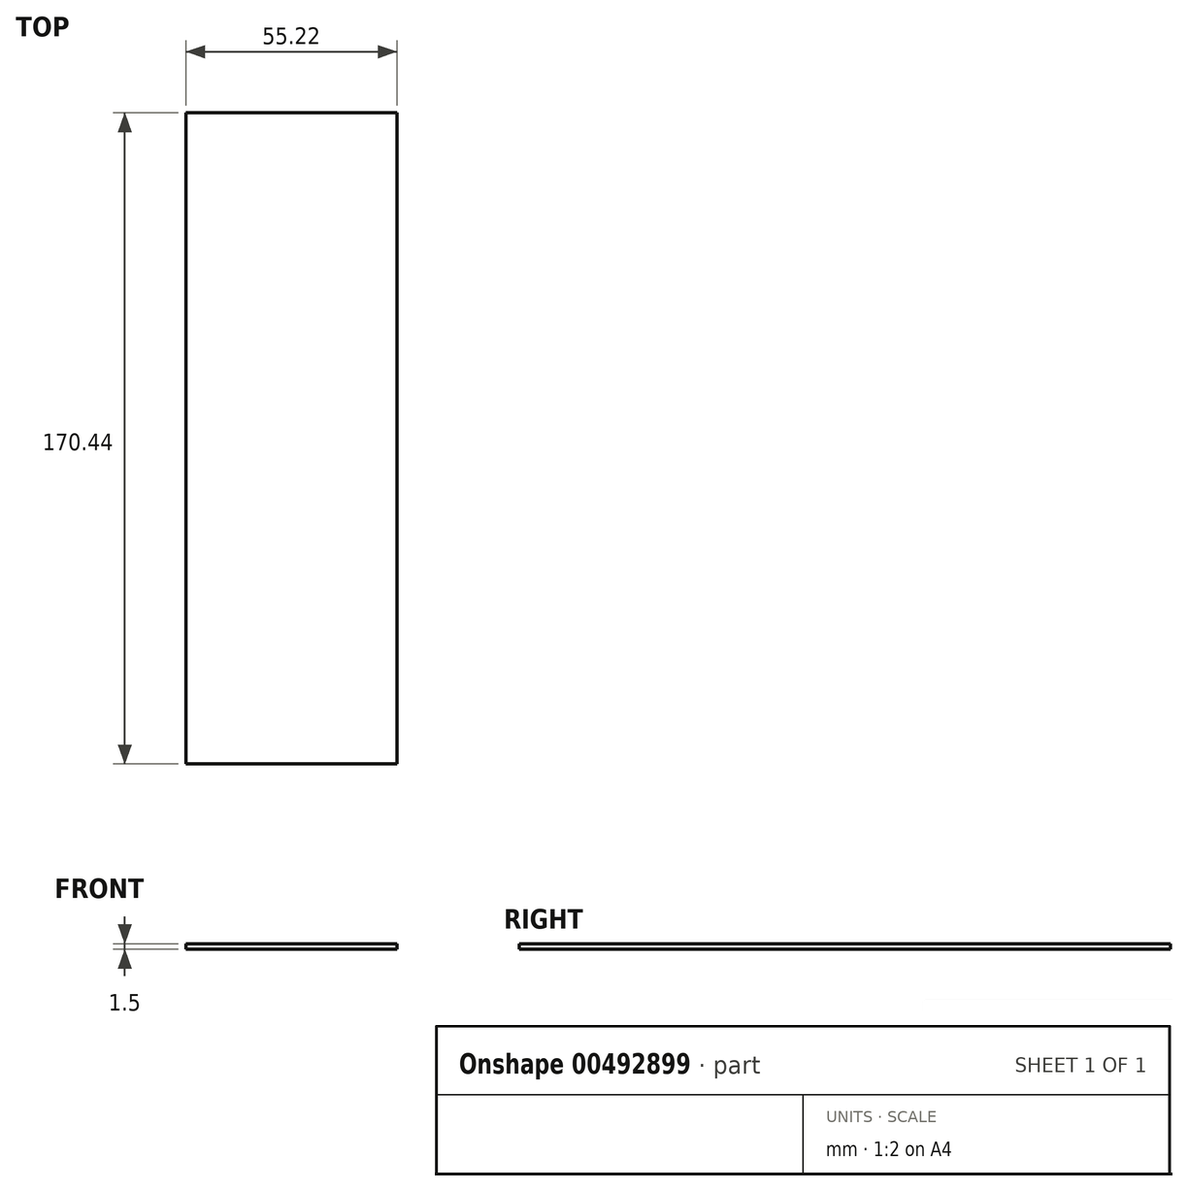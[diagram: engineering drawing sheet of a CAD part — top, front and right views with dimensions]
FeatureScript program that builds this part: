
annotation { "Feature Type Name" : "Feature", "Feature Type Description" : "" }
export const myFeature = defineFeature(function(context is Context, id is Id, definition is map)
    precondition{}
    {
        {
            var Q0;
            Q0=qCreatedBy(makeId("Top.planeOp"),FACE);
            var sketch = newSketch(context, id + "F0", { "sketchPlane" : qUnion([Q0])});
            skLineSegment(sketch, "E0.bottom", {"start": v(-25.98, -55.89) * mm, "end": v(29.24, -55.89) * mm});
            skLineSegment(sketch, "E0.top", {"start": v(-25.98, 114.55) * mm, "end": v(29.24, 114.55) * mm});
            skLineSegment(sketch, "E0.left", {"start": v(-25.98, -55.89) * mm, "end": v(-25.98, 114.55) * mm});
            skLineSegment(sketch, "E0.right", {"start": v(29.24, -55.89) * mm, "end": v(29.24, 114.55) * mm});
            skSolve(sketch);
        }
        {
            var Q0;
            Q0 = qSketchRegion(id + "F0", true);
            extrude(context, id + "F1", {"entities" : qUnion([Q0]), "depth" : 1.5 * mm});
        }
    });
